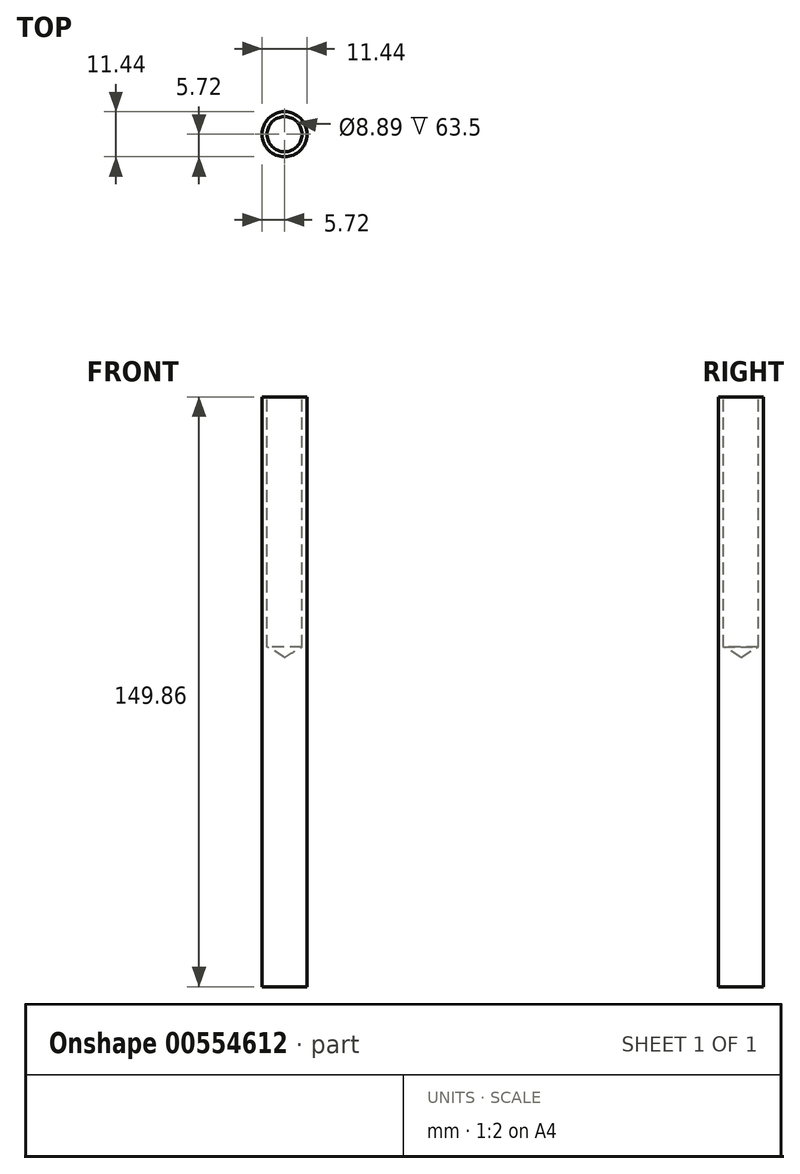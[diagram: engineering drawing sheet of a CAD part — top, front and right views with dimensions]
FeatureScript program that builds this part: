
annotation { "Feature Type Name" : "Feature", "Feature Type Description" : "" }
export const myFeature = defineFeature(function(context is Context, id is Id, definition is map)
    precondition{}
    {
        {
            var Q0;
            Q0=qCreatedBy(makeId("Top.planeOp"),FACE);
            var sketch = newSketch(context, id + "F0", { "sketchPlane" : qUnion([Q0])});
            skCircle(sketch, "E0", {"center": v(0, 0) * mm, "radius": 5.72 * mm});
            skSolve(sketch);
        }
        {
            var Q0;
            Q0=makeQuery(id+"F0.imprint","IMPRINT",FACE,{"disambiguationData":[TD([[makeQuery(id+"F0.imprint","IMPRINT",EDGE,{"derivedFrom":sQuery(id+"F0.wireOp",EDGE,"E0")}),1.0]])]});
            extrude(context, id + "F1", {"entities" : qUnion([Q0]), "depth" : 149.86 * mm});
        }
        {
            var Q0;
            Q0=makeQuery(id+"F1.opExtrude","CAP_FACE",FACE,{"disambiguationData":[OSD([sQuery(id+"F0.wireOp",EDGE,"E0")])],"isStart":false});
            var sketch = newSketch(context, id + "F2", { "sketchPlane" : qUnion([Q0])});
            skPoint(sketch, "E1", {"position": v(0, 0) * mm});
            skSolve(sketch);
        }
        {
            var Q0;
            Q0=sQuery(id+"F2.wireOp",VERTEX,"E1");
            var Q1;
            Q1=makeQuery(id+"F1.opExtrude","SWEPT_BODY",BODY,{"disambiguationData":[OSD([sQuery(id+"F0.wireOp",EDGE,"E0")])]});
            hole(context, id + "F3", {"style" : HoleStyle.SIMPLE, "endStyle" : HoleEndStyle.BLIND, "holeDiameter" : 8.9 * mm, "holeDepth" : 63.5 * mm, "isTappedThrough" : true, "tappedDepth" : 12.7 * mm, "tapClearance" : 3, "locations" : qUnion([Q0]), "scope" : qUnion([Q1]), "majorDiameter" : 6.35 * mm});
        }
    });
